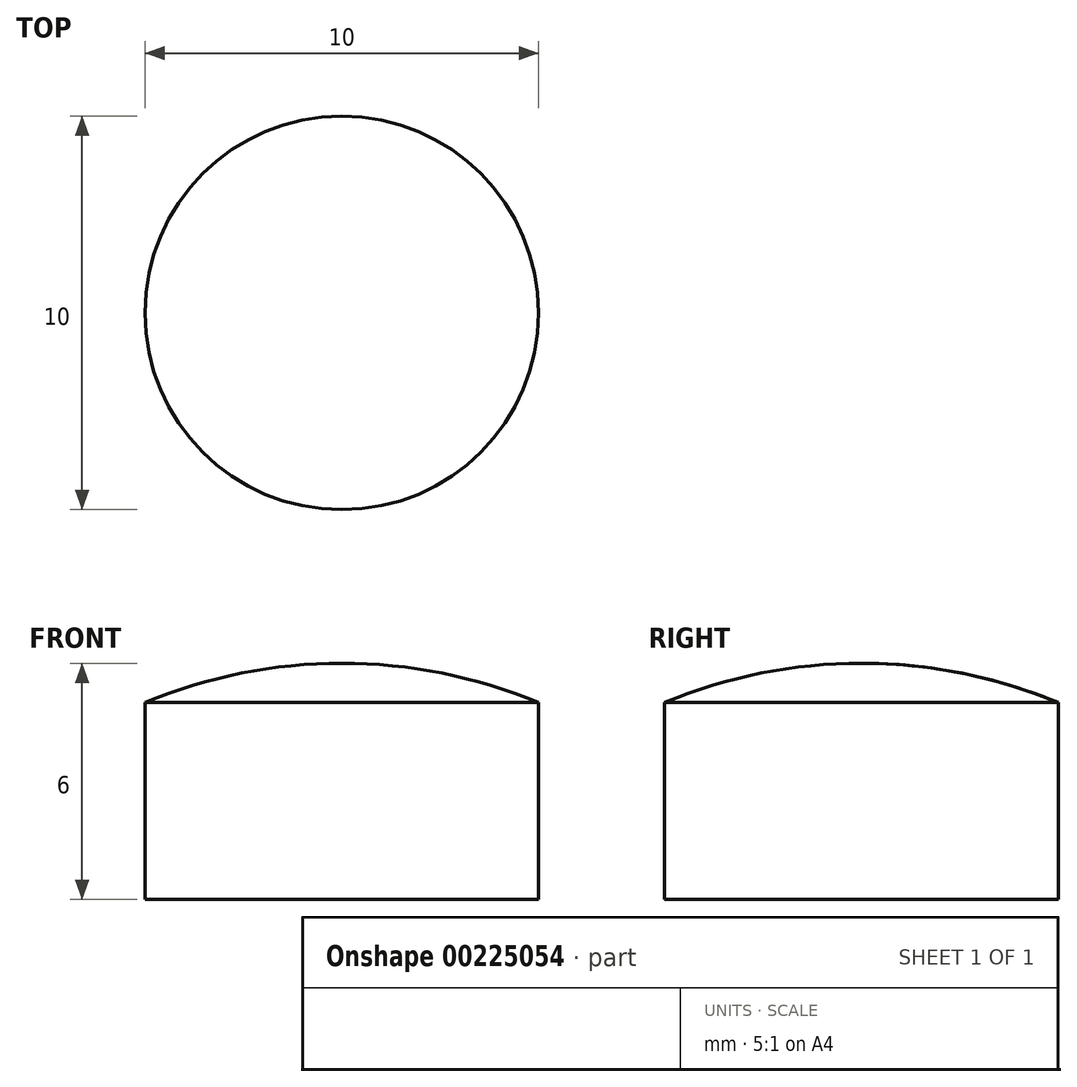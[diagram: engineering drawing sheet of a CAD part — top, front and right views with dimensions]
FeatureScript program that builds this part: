
annotation { "Feature Type Name" : "Feature", "Feature Type Description" : "" }
export const myFeature = defineFeature(function(context is Context, id is Id, definition is map)
    precondition{}
    {
        {
            var Q0;
            Q0=qCreatedBy(makeId("Top.planeOp"),FACE);
            var sketch = newSketch(context, id + "F0", { "sketchPlane" : qUnion([Q0])});
            skCircle(sketch, "E0", {"center": v(0, 0) * mm, "radius": 5 * mm});
            skSolve(sketch);
        }
        {
            var Q0;
            Q0 = qSketchRegion(id + "F0", true);
            extrude(context, id + "F1", {"entities" : qUnion([Q0]), "endBound" : BoundingType.SYMMETRIC, "depth" : 5 * mm});
        }
        {
            var Q0;
            Q0=qCreatedBy(makeId("Right.planeOp"),FACE);
            var sketch = newSketch(context, id + "F2", { "sketchPlane" : qUnion([Q0])});
            skArc(sketch, "E1", {"start": v(5, 2.5) * mm, "mid": v(2.55, 3.25) * mm, "end": v(0, 3.5) * mm});
            skLineSegment(sketch, "E2", {"start": v(0, 3.5) * mm, "end": v(0, 2.5) * mm});
            skLineSegment(sketch, "E3", {"start": v(0, 2.5) * mm, "end": v(5, 2.5) * mm});
            skPoint(sketch, "E4.orphan", {"position": v(-5, 2.5) * mm});
            skArc(sketch, "E5.MirrorCS", {"start": v(5, -2.5) * mm, "mid": v(2.55, -3.25) * mm, "end": v(0, -3.5) * mm});
            skLineSegment(sketch, "E6.MirrorCS", {"start": v(0, -2.5) * mm, "end": v(5, -2.5) * mm});
            skLineSegment(sketch, "E7.MirrorCS", {"start": v(0, -3.5) * mm, "end": v(0, -2.5) * mm});
            skSolve(sketch);
        }
        {
            var Q0;
            Q0=makeQuery(id+"F2.imprint","IMPRINT",FACE,{"disambiguationData":[TD([[makeQuery(id+"F2.imprint","IMPRINT",EDGE,{"derivedFrom":sQuery(id+"F2.wireOp",EDGE,"E1")}),1.0]])]});
            var Q1;
            Q1=makeQuery(id+"F2.imprint","IMPRINT",FACE,{"disambiguationData":[TD([[makeQuery(id+"F2.imprint","IMPRINT",EDGE,{"derivedFrom":sQuery(id+"F2.wireOp",EDGE,"E5.MirrorCS")}),-1.0]])]});
            var Q2;
            Q2=sQuery(id+"F2.wireOp",EDGE,"E2");
            revolve(context, id + "F3", {"operationType" : NewBodyOperationType.ADD, "entities" : qUnion([Q0, Q1]), "axis" : qUnion([Q2]), "revolveType" : RevolveType.FULL});
        }
    });
